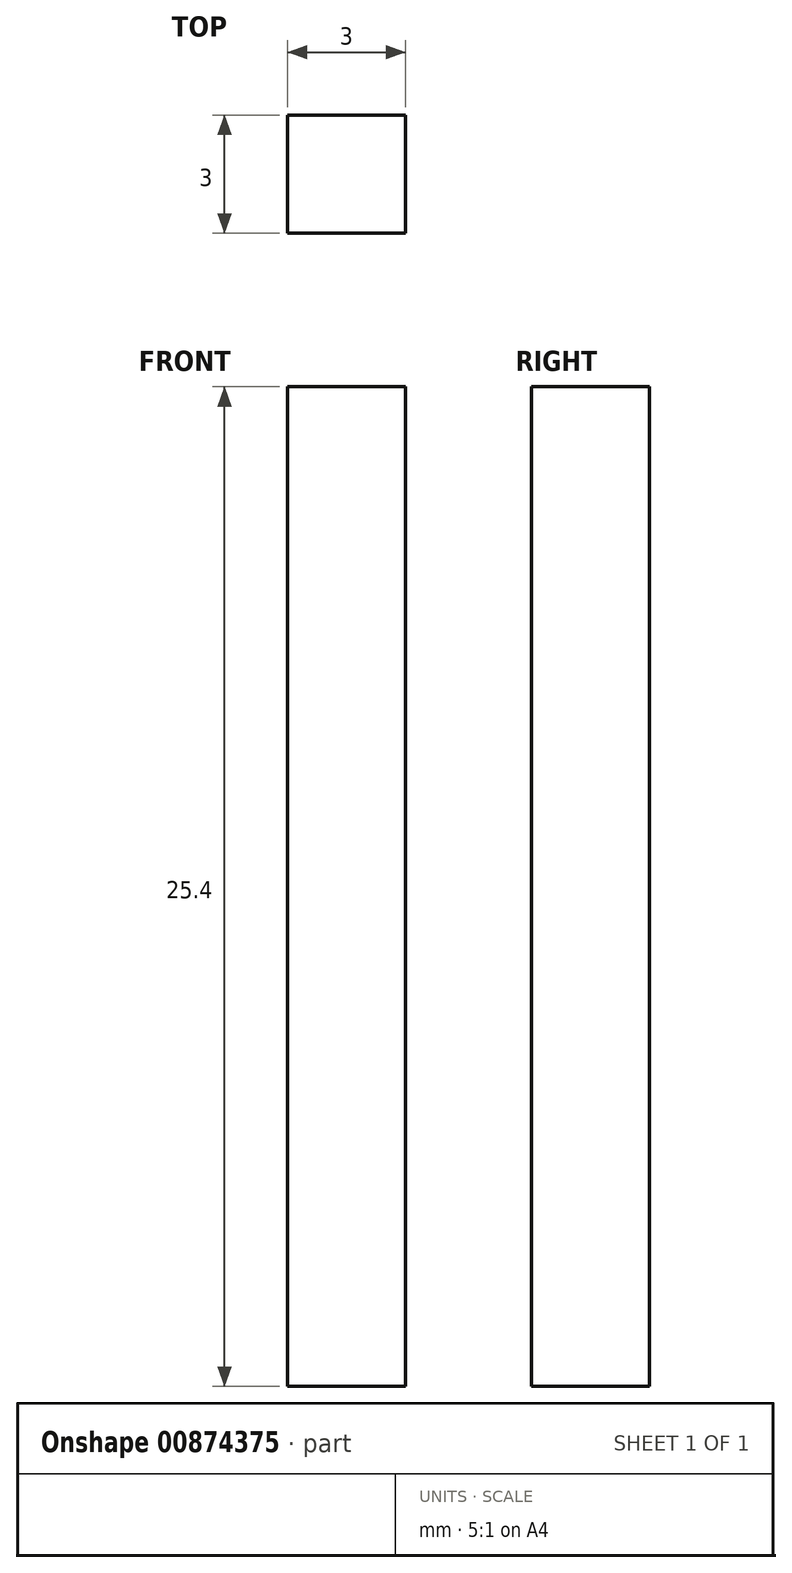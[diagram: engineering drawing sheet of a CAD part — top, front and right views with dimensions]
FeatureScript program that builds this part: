
annotation { "Feature Type Name" : "Feature", "Feature Type Description" : "" }
export const myFeature = defineFeature(function(context is Context, id is Id, definition is map)
    precondition{}
    {
        {
            var Q0;
            Q0=qCreatedBy(makeId("Top.planeOp"),FACE);
            var sketch = newSketch(context, id + "F0", { "sketchPlane" : qUnion([Q0])});
            skLineSegment(sketch, "E0.bottom", {"start": v(1.5, 1.5) * mm, "end": v(-1.5, 1.5) * mm});
            skLineSegment(sketch, "E0.top", {"start": v(1.5, -1.5) * mm, "end": v(-1.5, -1.5) * mm});
            skLineSegment(sketch, "E0.left", {"start": v(1.5, 1.5) * mm, "end": v(1.5, -1.5) * mm});
            skLineSegment(sketch, "E0.right", {"start": v(-1.5, 1.5) * mm, "end": v(-1.5, -1.5) * mm});
            skPoint(sketch, "E0.middle", {"position": v(0, 0) * mm});
            skSolve(sketch);
        }
        {
            var Q0;
            Q0=makeQuery(id+"F0.imprint","IMPRINT",FACE,{"disambiguationData":[TD([[makeQuery(id+"F0.imprint","IMPRINT",EDGE,{"derivedFrom":sQuery(id+"F0.wireOp",EDGE,"E0.bottom")}),1.0]])]});
            extrude(context, id + "F1", {"entities" : qUnion([Q0]), "depth" : 25.4 * mm, "offsetDistance" : 25.4 * mm});
        }
    });
